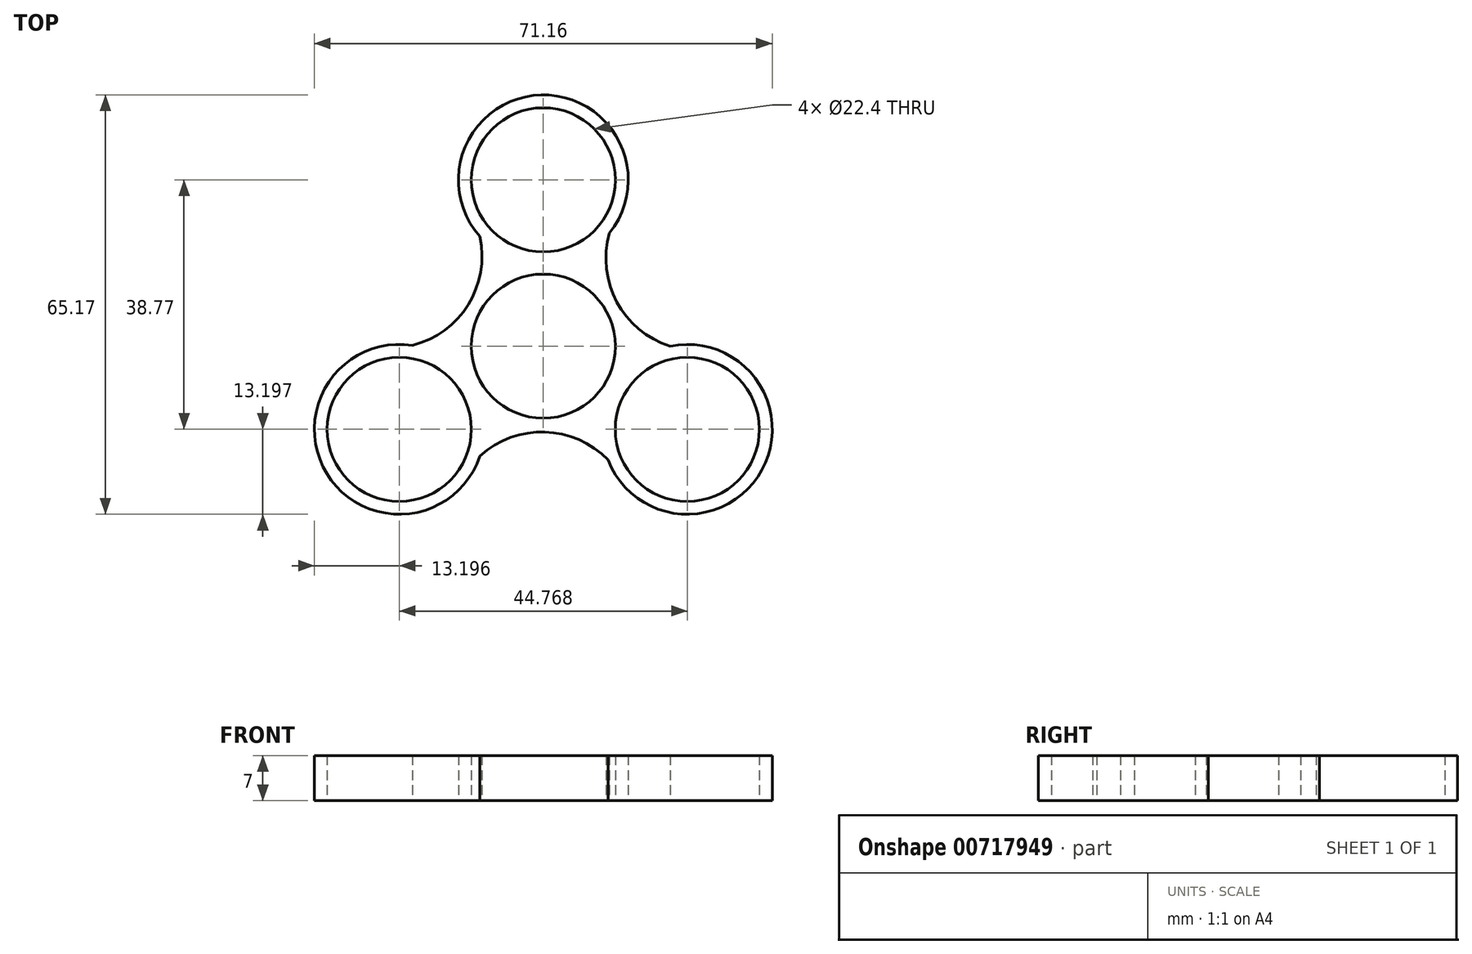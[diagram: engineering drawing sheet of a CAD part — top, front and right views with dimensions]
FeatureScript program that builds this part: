
annotation { "Feature Type Name" : "Feature", "Feature Type Description" : "" }
export const myFeature = defineFeature(function(context is Context, id is Id, definition is map)
    precondition{}
    {
        {
            var Q0;
            Q0=qCreatedBy(makeId("Top.planeOp"),FACE);
            var sketch = newSketch(context, id + "F0", { "sketchPlane" : qUnion([Q0])});
            skCircle(sketch, "E0", {"center": v(0, 0) * mm, "radius": 11.2 * mm});
            skCircle(sketch, "E1", {"center": v(0, 25.85) * mm, "radius": 11.2 * mm});
            skArc(sketch, "E2.1.0", {"start": v(-20.35, 0.12) * mm, "mid": v(-33.65, -19.81) * mm, "end": v(-9.85, -17.06) * mm});
            skCircle(sketch, "E2.1.1", {"center": v(-22.38, -12.92) * mm, "radius": 11.2 * mm});
            skArc(sketch, "E2.2.0", {"start": v(10.07, -17.69) * mm, "mid": v(33.98, -19.23) * mm, "end": v(19.7, 0) * mm});
            skCircle(sketch, "E2.2.1", {"center": v(22.38, -12.92) * mm, "radius": 11.2 * mm});
            skArc(sketch, "E3", {"start": v(10.28, 17.57) * mm, "mid": v(11.43, 6.88) * mm, "end": v(19.7, 0) * mm});
            skArc(sketch, "E4.1.0", {"start": v(-20.35, 0.12) * mm, "mid": v(-11.67, 6.46) * mm, "end": v(-9.85, 17.06) * mm});
            skArc(sketch, "E4.2.0", {"start": v(10.07, -17.69) * mm, "mid": v(0.24, -13.34) * mm, "end": v(-9.85, -17.06) * mm});
            skArc(sketch, "E5.trimOffspring", {"start": v(10.28, 17.57) * mm, "mid": v(-0.33, 39.04) * mm, "end": v(-9.85, 17.06) * mm});
            skSolve(sketch);
        }
        {
            var Q0;
            Q0=makeQuery(id+"F0.imprint","IMPRINT",FACE,{"disambiguationData":[TD([[makeQuery(id+"F0.imprint","IMPRINT",EDGE,{"derivedFrom":sQuery(id+"F0.wireOp",EDGE,"E0")}),-1.0]])]});
            extrude(context, id + "F1", {"entities" : qUnion([Q0]), "depth" : 7 * mm, "offsetDistance" : 25 * mm});
        }
    });
